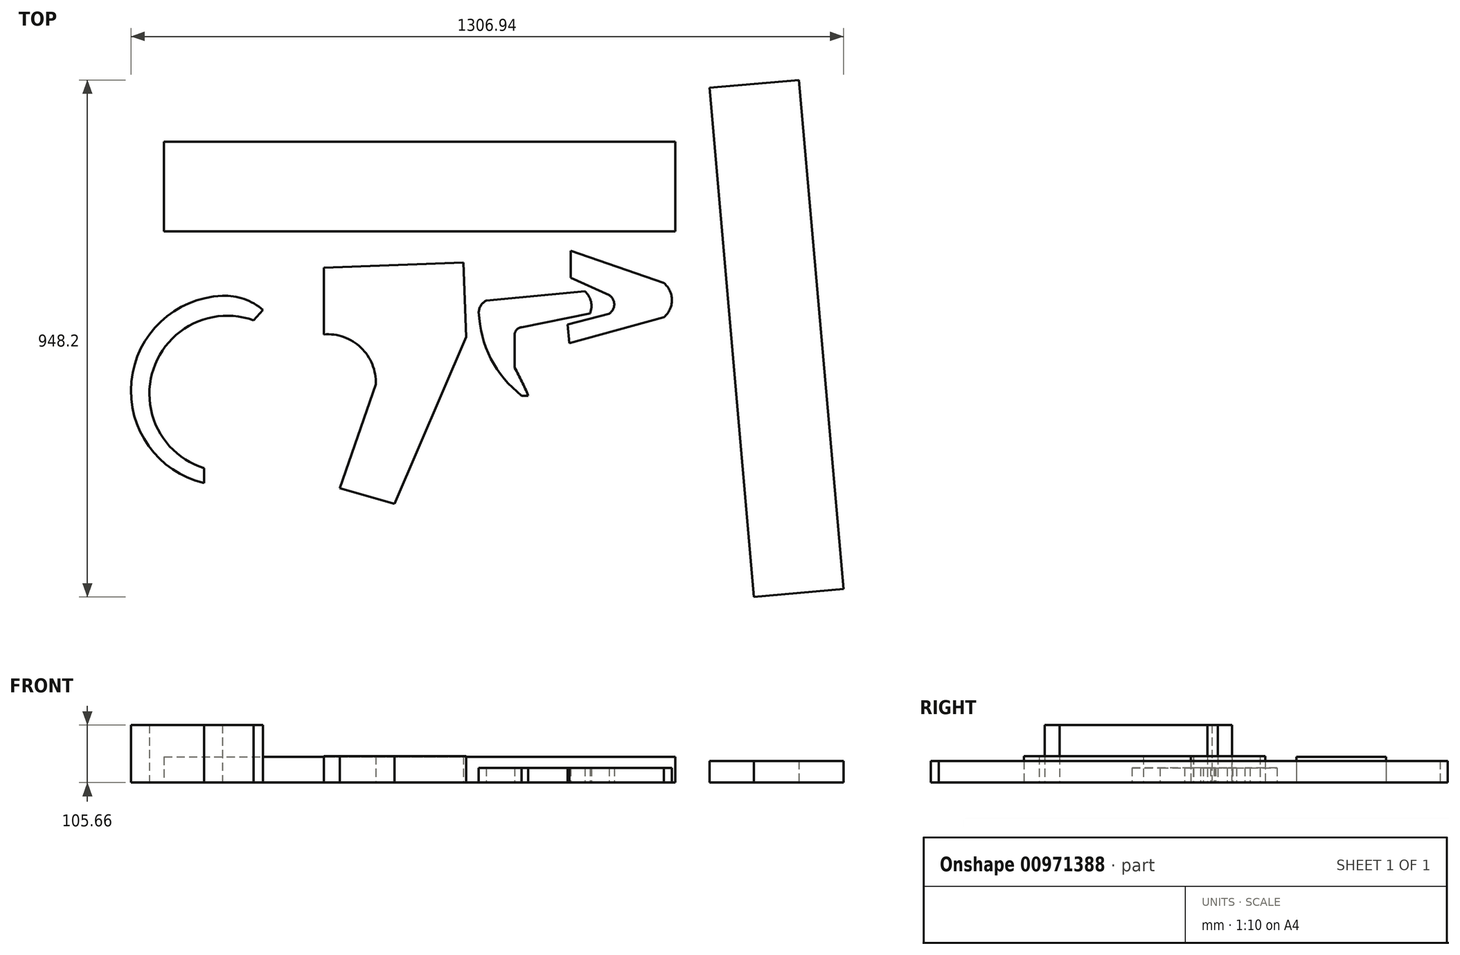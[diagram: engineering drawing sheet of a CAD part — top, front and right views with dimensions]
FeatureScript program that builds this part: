
annotation { "Feature Type Name" : "Feature", "Feature Type Description" : "" }
export const myFeature = defineFeature(function(context is Context, id is Id, definition is map)
    precondition{}
    {
        {
            var Q0;
            Q0=qCreatedBy(makeId("Top.planeOp"),FACE);
            var sketch = newSketch(context, id + "F0", { "sketchPlane" : qUnion([Q0])});
            skArc(sketch, "E0", {"start": v(-184.13, 4.56) * mm, "mid": v(-161.86, -80.93) * mm, "end": v(-105.38, -148.86) * mm});
            skLineSegment(sketch, "E1", {"start": v(-105.38, -148.86) * mm, "end": v(-93.39, -148.86) * mm});
            skArc(sketch, "E2", {"start": v(-93.39, -148.86) * mm, "mid": v(-105.11, -122.87) * mm, "end": v(-118.17, -97.52) * mm});
            skLineSegment(sketch, "E3", {"start": v(-118.17, -97.52) * mm, "end": v(-118.17, -36.45) * mm});
            skArc(sketch, "E4", {"start": v(-105.27, -23.52) * mm, "mid": v(-114.4, -27.31) * mm, "end": v(-118.17, -36.45) * mm});
            skLineSegment(sketch, "E5", {"start": v(-105.27, -23.52) * mm, "end": v(19.88, 1.92) * mm});
            skArc(sketch, "E6", {"start": v(19.88, 1.92) * mm, "mid": v(21.7, 23.77) * mm, "end": v(10.32, 42.52) * mm});
            skLineSegment(sketch, "E7", {"start": v(10.32, 42.52) * mm, "end": v(-170.32, 25.71) * mm});
            skArc(sketch, "E8", {"start": v(-170.32, 25.71) * mm, "mid": v(-179.98, 16.94) * mm, "end": v(-184.13, 4.56) * mm});
            skLineSegment(sketch, "E9", {"start": v(-21.39, -18.31) * mm, "end": v(54.7, 1.44) * mm});
            skArc(sketch, "E10", {"start": v(54.7, 1.44) * mm, "mid": v(64.3, 18.59) * mm, "end": v(54.7, 35.73) * mm});
            skLineSegment(sketch, "E11", {"start": v(54.7, 35.73) * mm, "end": v(-15.32, 67.43) * mm});
            skLineSegment(sketch, "E12", {"start": v(-15.32, 67.43) * mm, "end": v(-15.32, 117.16) * mm});
            skLineSegment(sketch, "E13", {"start": v(-15.32, 117.16) * mm, "end": v(155.26, 57.8) * mm});
            skArc(sketch, "E14", {"start": v(155.26, -5.02) * mm, "mid": v(170.08, 26.39) * mm, "end": v(155.26, 57.8) * mm});
            skLineSegment(sketch, "E15", {"start": v(155.26, -5.02) * mm, "end": v(-18.23, -52.6) * mm});
            skLineSegment(sketch, "E16", {"start": v(-21.39, -18.31) * mm, "end": v(-18.23, -52.6) * mm});
            skLineSegment(sketch, "E17", {"start": v(-468.42, 85.92) * mm, "end": v(-468.42, -36.45) * mm});
            skLineSegment(sketch, "E18", {"start": v(-468.42, 85.92) * mm, "end": v(-212.08, 95.4) * mm});
            skLineSegment(sketch, "E19", {"start": v(-212.08, 95.4) * mm, "end": v(-207.03, -40.93) * mm});
            skLineSegment(sketch, "E20", {"start": v(-207.03, -40.93) * mm, "end": v(-338.48, -347.33) * mm});
            skLineSegment(sketch, "E21", {"start": v(-338.48, -347.33) * mm, "end": v(-439.24, -318.92) * mm});
            skLineSegment(sketch, "E22", {"start": v(-439.24, -318.92) * mm, "end": v(-373.04, -127.93) * mm});
            skArc(sketch, "E23", {"start": v(-373.04, -127.93) * mm, "mid": v(-400.2, -60.8) * mm, "end": v(-468.42, -36.45) * mm});
            skLineSegment(sketch, "E24.bottom", {"start": v(-761.38, 317.09) * mm, "end": v(176.03, 317.09) * mm});
            skLineSegment(sketch, "E24.top", {"start": v(-761.38, 152.36) * mm, "end": v(176.03, 152.36) * mm});
            skLineSegment(sketch, "E24.left", {"start": v(-761.38, 317.09) * mm, "end": v(-761.38, 152.36) * mm});
            skLineSegment(sketch, "E24.right", {"start": v(176.03, 317.09) * mm, "end": v(176.03, 152.36) * mm});
            skLineSegment(sketch, "E25.bottom", {"start": v(320.78, -517.99) * mm, "end": v(239.08, 415.85) * mm});
            skLineSegment(sketch, "E25.top", {"start": v(484.88, -503.63) * mm, "end": v(403.18, 430.2) * mm});
            skLineSegment(sketch, "E25.left", {"start": v(320.78, -517.99) * mm, "end": v(484.88, -503.63) * mm});
            skLineSegment(sketch, "E25.right", {"start": v(239.08, 415.85) * mm, "end": v(403.18, 430.2) * mm});
            skArc(sketch, "E26", {"start": v(-654.52, 34.18) * mm, "mid": v(-821.24, -122.88) * mm, "end": v(-687.97, -309.17) * mm});
            skArc(sketch, "E27", {"start": v(-579.8, 8.24) * mm, "mid": v(-614.62, 28.52) * mm, "end": v(-654.52, 34.18) * mm});
            skLineSegment(sketch, "E28", {"start": v(-687.97, -309.17) * mm, "end": v(-687.97, -282) * mm});
            skLineSegment(sketch, "E29", {"start": v(-579.8, 8.24) * mm, "end": v(-597, -10.69) * mm});
            skArc(sketch, "E30", {"start": v(-597, -10.69) * mm, "mid": v(-780.84, -99.95) * mm, "end": v(-687.97, -282) * mm});
            skSolve(sketch);
        }
        {
            var Q0;
            Q0 = qSketchRegion(id + "F0", true);
            extrude(context, id + "F1", {"entities" : qUnion([Q0]), "depth" : 26.92 * mm, "offsetDistance" : 25.4 * mm});
        }
        {
            var Q0;
            Q0=makeQuery(id+"F1.opExtrude","CAP_FACE",FACE,{"disambiguationData":[OSD([sQuery(id+"F0.wireOp",EDGE,"E17"),sQuery(id+"F0.wireOp",EDGE,"E18"),sQuery(id+"F0.wireOp",EDGE,"E19"),sQuery(id+"F0.wireOp",EDGE,"E20"),sQuery(id+"F0.wireOp",EDGE,"E21"),sQuery(id+"F0.wireOp",EDGE,"E22"),sQuery(id+"F0.wireOp",EDGE,"E23")])],"isStart":false});
            extrude(context, id + "F2", {"entities" : qUnion([Q0]), "operationType" : NewBodyOperationType.ADD, "depth" : 21.59 * mm, "offsetDistance" : 25.4 * mm});
        }
        {
            var Q0;
            Q0=makeQuery(id+"F1.opExtrude","CAP_FACE",FACE,{"disambiguationData":[OSD([sQuery(id+"F0.wireOp",EDGE,"E25.bottom"),sQuery(id+"F0.wireOp",EDGE,"E25.top"),sQuery(id+"F0.wireOp",EDGE,"E25.left"),sQuery(id+"F0.wireOp",EDGE,"E25.right")])],"isStart":false});
            extrude(context, id + "F3", {"entities" : qUnion([Q0]), "operationType" : NewBodyOperationType.ADD, "depth" : 12.7 * mm, "offsetDistance" : 25.4 * mm});
        }
        {
            var Q0;
            Q0=makeQuery(id+"F1.opExtrude","CAP_FACE",FACE,{"disambiguationData":[OSD([sQuery(id+"F0.wireOp",EDGE,"E24.bottom"),sQuery(id+"F0.wireOp",EDGE,"E24.top"),sQuery(id+"F0.wireOp",EDGE,"E24.left"),sQuery(id+"F0.wireOp",EDGE,"E24.right")])],"isStart":false});
            extrude(context, id + "F4", {"entities" : qUnion([Q0]), "operationType" : NewBodyOperationType.ADD, "depth" : 20.32 * mm, "offsetDistance" : 25.4 * mm});
        }
        {
            var Q0;
            Q0=makeQuery(id+"F1.opExtrude","CAP_FACE",FACE,{"disambiguationData":[OSD([sQuery(id+"F0.wireOp",EDGE,"E26"),sQuery(id+"F0.wireOp",EDGE,"E27"),sQuery(id+"F0.wireOp",EDGE,"E28"),sQuery(id+"F0.wireOp",EDGE,"E29"),sQuery(id+"F0.wireOp",EDGE,"E30")])],"isStart":false});
            extrude(context, id + "F5", {"entities" : qUnion([Q0]), "operationType" : NewBodyOperationType.ADD, "depth" : 78.74 * mm, "offsetDistance" : 25.4 * mm});
        }
    });
